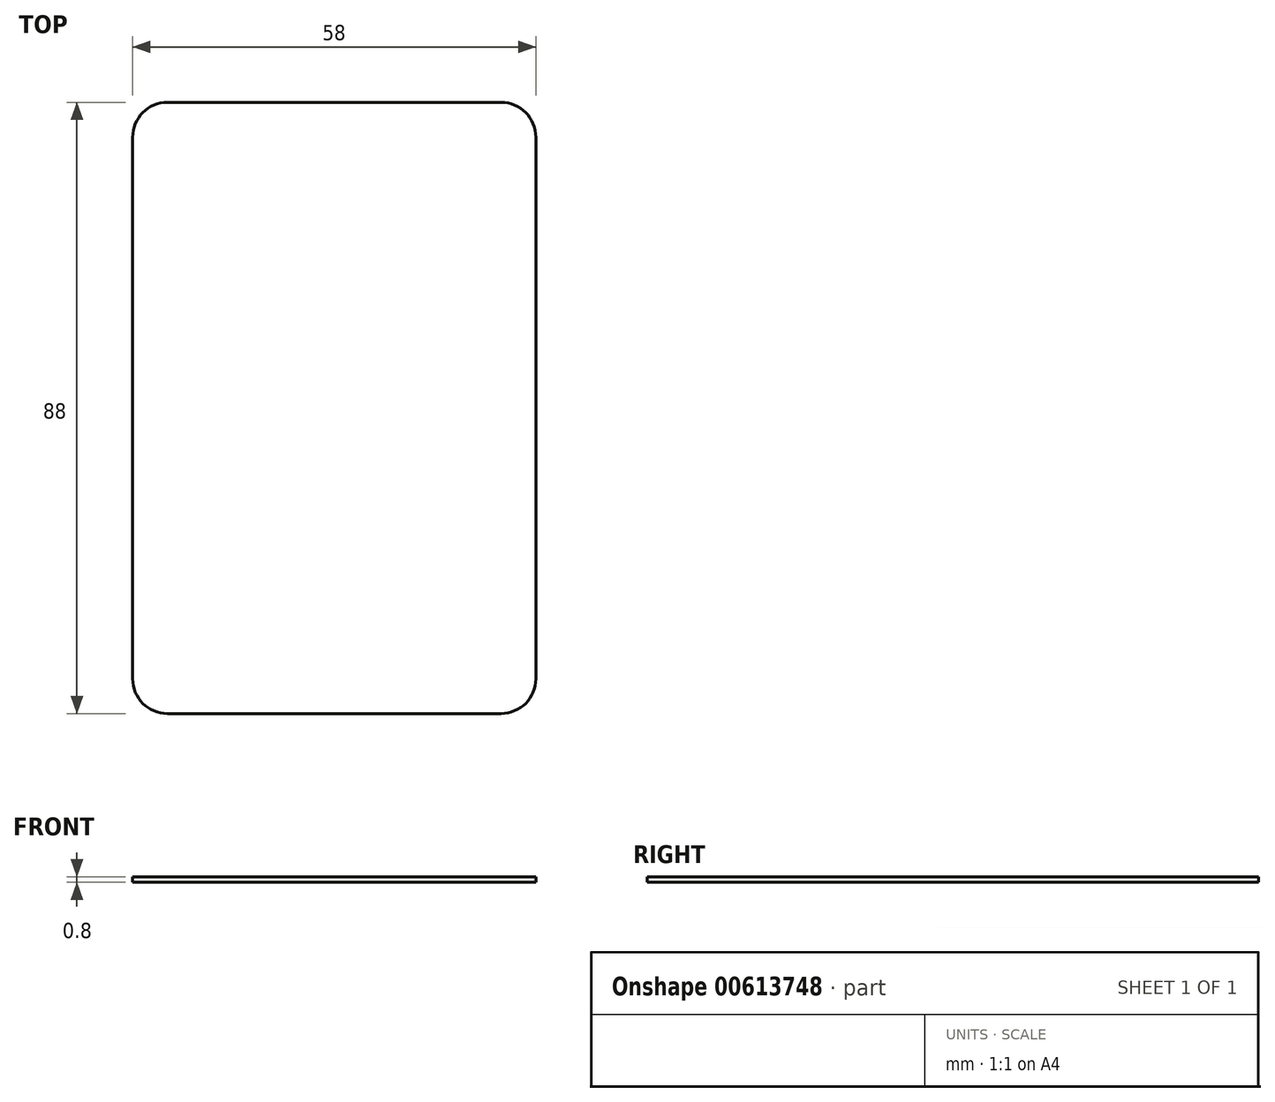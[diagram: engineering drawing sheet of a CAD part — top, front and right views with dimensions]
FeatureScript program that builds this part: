
annotation { "Feature Type Name" : "Feature", "Feature Type Description" : "" }
export const myFeature = defineFeature(function(context is Context, id is Id, definition is map)
    precondition{}
    {
        {
            var Q0;
            Q0=qCreatedBy(makeId("Top.planeOp"),FACE);
            var sketch = newSketch(context, id + "F0", { "sketchPlane" : qUnion([Q0])});
            skLineSegment(sketch, "E0.bottom", {"start": v(-5, 0) * mm, "end": v(-53, 0) * mm});
            skLineSegment(sketch, "E0.top", {"start": v(-5, 88) * mm, "end": v(-53, 88) * mm});
            skLineSegment(sketch, "E0.left", {"start": v(0, 5) * mm, "end": v(0, 83) * mm});
            skLineSegment(sketch, "E0.right", {"start": v(-58, 5) * mm, "end": v(-58, 83) * mm});
            skPoint(sketch, "E1.visualSharp", {"position": v(-58, 0) * mm});
            skArc(sketch, "E1.filletArc", {"start": v(-58, 5) * mm, "mid": v(-56.54, 1.46) * mm, "end": v(-53, 0) * mm});
            skPoint(sketch, "E2.visualSharp", {"position": v(0, 0) * mm});
            skArc(sketch, "E2.filletArc", {"start": v(-5, 0) * mm, "mid": v(-1.46, 1.46) * mm, "end": v(0, 5) * mm});
            skPoint(sketch, "E3.visualSharp", {"position": v(-58, 88) * mm});
            skArc(sketch, "E3.filletArc", {"start": v(-53, 88) * mm, "mid": v(-56.54, 86.54) * mm, "end": v(-58, 83) * mm});
            skPoint(sketch, "E4.visualSharp", {"position": v(0, 88) * mm});
            skArc(sketch, "E4.filletArc", {"start": v(0, 83) * mm, "mid": v(-1.46, 86.54) * mm, "end": v(-5, 88) * mm});
            skSolve(sketch);
        }
        {
            var Q0;
            Q0=makeQuery(id+"F0.imprint","IMPRINT",FACE,{"disambiguationData":[TD([[makeQuery(id+"F0.imprint","IMPRINT",EDGE,{"derivedFrom":sQuery(id+"F0.wireOp",EDGE,"E0.bottom")}),-1.0]])]});
            extrude(context, id + "F1", {"entities" : qUnion([Q0]), "depth" : 0.8 * mm, "offsetDistance" : 25 * mm});
        }
    });
